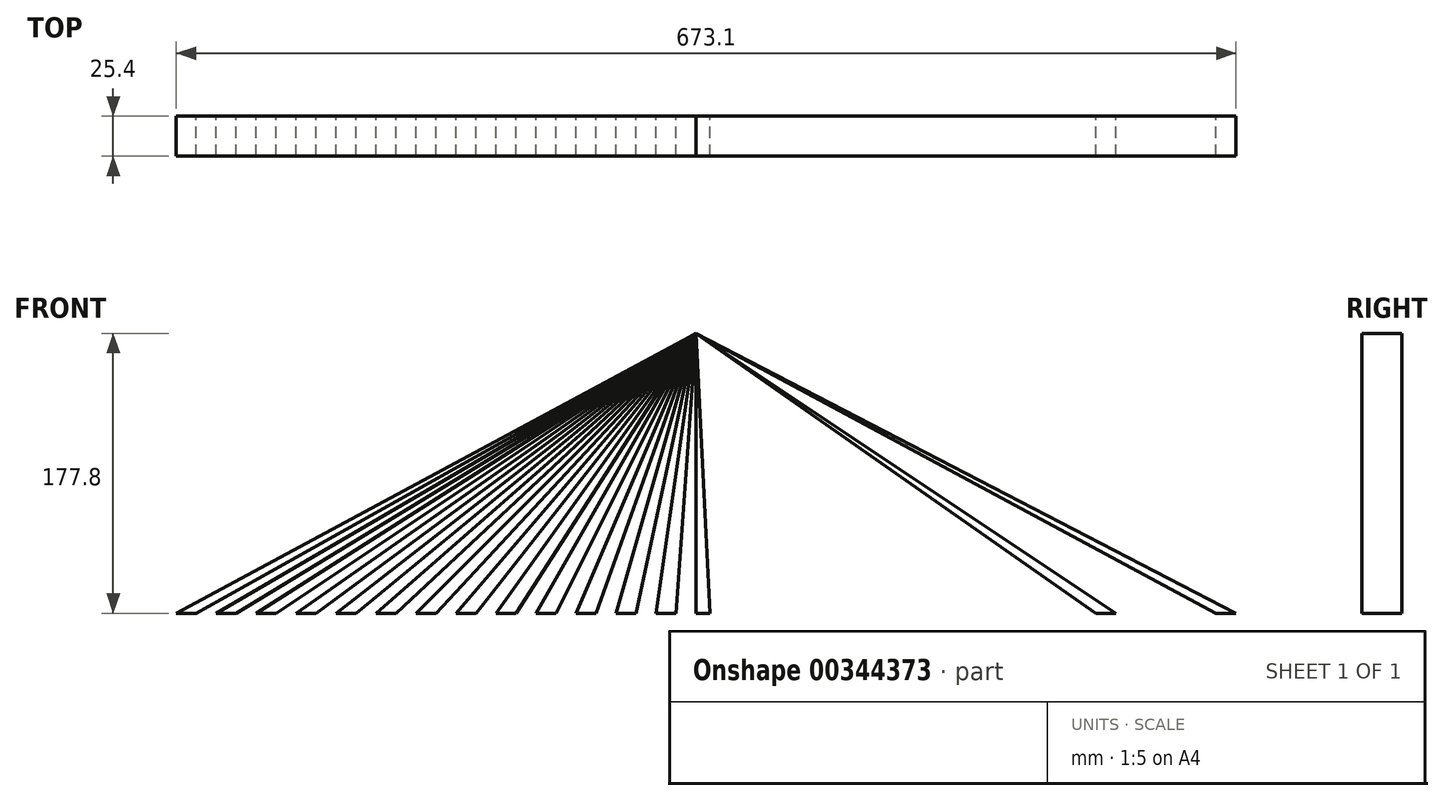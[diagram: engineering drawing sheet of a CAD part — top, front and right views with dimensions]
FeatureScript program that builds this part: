
annotation { "Feature Type Name" : "Feature", "Feature Type Description" : "" }
export const myFeature = defineFeature(function(context is Context, id is Id, definition is map)
    precondition{}
    {
        {
            var Q0;
            Q0=qCreatedBy(makeId("Front.planeOp"),FACE);
            var sketch = newSketch(context, id + "F0", { "sketchPlane" : qUnion([Q0])});
            skLineSegment(sketch, "E0", {"start": v(78.5, 0) * mm, "end": v(-175.5, 0) * mm});
            skLineSegment(sketch, "E1", {"start": v(-175.5, 0) * mm, "end": v(-175.5, 177.8) * mm});
            skLineSegment(sketch, "E2", {"start": v(-175.5, 177.8) * mm, "end": v(78.5, 0) * mm});
            skLineSegment(sketch, "E3", {"start": v(78.5, 0) * mm, "end": v(64.1, 0) * mm});
            skLineSegment(sketch, "E4", {"start": v(64.1, 0) * mm, "end": v(51.4, 0) * mm});
            skLineSegment(sketch, "E5", {"start": v(51.4, 0) * mm, "end": v(38.7, 0) * mm});
            skLineSegment(sketch, "E6", {"start": v(38.7, 0) * mm, "end": v(26, 0) * mm});
            skLineSegment(sketch, "E7", {"start": v(26, 0) * mm, "end": v(12.7, 0) * mm});
            skLineSegment(sketch, "E8", {"start": v(12.7, 0) * mm, "end": v(0, 0) * mm});
            skLineSegment(sketch, "E9", {"start": v(0, 0) * mm, "end": v(-12.7, 0) * mm});
            skLineSegment(sketch, "E10", {"start": v(-12.7, 0) * mm, "end": v(-25.4, 0) * mm});
            skLineSegment(sketch, "E11", {"start": v(-25.4, 0) * mm, "end": v(-38.1, 0) * mm});
            skLineSegment(sketch, "E12", {"start": v(-38.1, 0) * mm, "end": v(-48.5, 0) * mm});
            skLineSegment(sketch, "E13", {"start": v(-48.5, 0) * mm, "end": v(-64.04, 0) * mm});
            skLineSegment(sketch, "E14", {"start": v(-64.04, 0) * mm, "end": v(-77.66, 0) * mm});
            skLineSegment(sketch, "E15", {"start": v(-77.66, 0) * mm, "end": v(-89.19, 0) * mm});
            skLineSegment(sketch, "E16", {"start": v(-89.19, 0) * mm, "end": v(-102.8, 0) * mm});
            skLineSegment(sketch, "E17", {"start": v(-102.8, 0) * mm, "end": v(-118.17, 0) * mm});
            skLineSegment(sketch, "E18", {"start": v(-118.17, 0) * mm, "end": v(-131.45, 0) * mm});
            skLineSegment(sketch, "E19", {"start": v(-131.45, 0) * mm, "end": v(-144.02, 0) * mm});
            skLineSegment(sketch, "E20", {"start": v(-144.02, 0) * mm, "end": v(-155.55, 0) * mm});
            skLineSegment(sketch, "E21", {"start": v(-155.55, 0) * mm, "end": v(-166.72, 0) * mm});
            skLineSegment(sketch, "E22", {"start": v(-166.72, 0) * mm, "end": v(-175.5, 0) * mm});
            skLineSegment(sketch, "E23", {"start": v(-175.5, 177.8) * mm, "end": v(64.1, 0) * mm});
            skLineSegment(sketch, "E24", {"start": v(-175.5, 177.8) * mm, "end": v(51.4, 0) * mm});
            skLineSegment(sketch, "E25", {"start": v(-175.5, 177.8) * mm, "end": v(38.7, 0) * mm});
            skLineSegment(sketch, "E26", {"start": v(-175.5, 177.8) * mm, "end": v(26, 0) * mm});
            skLineSegment(sketch, "E27", {"start": v(-175.5, 177.8) * mm, "end": v(12.7, 0) * mm});
            skLineSegment(sketch, "E28", {"start": v(-175.5, 177.8) * mm, "end": v(0, 0) * mm});
            skLineSegment(sketch, "E29", {"start": v(-175.5, 177.8) * mm, "end": v(-12.7, 0) * mm});
            skLineSegment(sketch, "E30", {"start": v(-175.5, 177.8) * mm, "end": v(-25.4, 0) * mm});
            skLineSegment(sketch, "E31", {"start": v(-175.5, 177.8) * mm, "end": v(-38.1, 0) * mm});
            skLineSegment(sketch, "E32", {"start": v(-175.5, 177.8) * mm, "end": v(-48.5, 0) * mm});
            skLineSegment(sketch, "E33", {"start": v(-175.5, 177.8) * mm, "end": v(-64.04, 0) * mm});
            skLineSegment(sketch, "E34", {"start": v(-175.5, 177.8) * mm, "end": v(-77.66, 0) * mm});
            skLineSegment(sketch, "E35", {"start": v(-175.5, 177.8) * mm, "end": v(-89.19, 0) * mm});
            skLineSegment(sketch, "E36", {"start": v(-175.5, 177.8) * mm, "end": v(-102.8, 0) * mm});
            skLineSegment(sketch, "E37", {"start": v(-175.5, 177.8) * mm, "end": v(-118.17, 0) * mm});
            skLineSegment(sketch, "E38", {"start": v(-175.5, 177.8) * mm, "end": v(-131.45, 0) * mm});
            skLineSegment(sketch, "E39", {"start": v(-175.5, 177.8) * mm, "end": v(-144.02, 0) * mm});
            skLineSegment(sketch, "E40", {"start": v(-175.5, 177.8) * mm, "end": v(-155.55, 0) * mm});
            skLineSegment(sketch, "E41", {"start": v(-175.5, 177.8) * mm, "end": v(-166.72, 0) * mm});
            skLineSegment(sketch, "E42", {"start": v(78.5, 0) * mm, "end": v(154.7, 0) * mm});
            skLineSegment(sketch, "E43", {"start": v(78.5, 0) * mm, "end": v(91.2, 0) * mm});
            skLineSegment(sketch, "E44", {"start": v(91.2, 0) * mm, "end": v(103.9, 0) * mm});
            skLineSegment(sketch, "E45", {"start": v(103.9, 0) * mm, "end": v(116.6, 0) * mm});
            skLineSegment(sketch, "E46", {"start": v(116.6, 0) * mm, "end": v(129.3, 0) * mm});
            skLineSegment(sketch, "E47", {"start": v(129.3, 0) * mm, "end": v(142, 0) * mm});
            skLineSegment(sketch, "E48", {"start": v(-175.5, 177.8) * mm, "end": v(91.2, 0) * mm});
            skLineSegment(sketch, "E49", {"start": v(-175.5, 177.8) * mm, "end": v(103.9, 0) * mm});
            skLineSegment(sketch, "E50", {"start": v(-175.5, 177.8) * mm, "end": v(116.6, 0) * mm});
            skLineSegment(sketch, "E51", {"start": v(-175.5, 177.8) * mm, "end": v(129.3, 0) * mm});
            skLineSegment(sketch, "E52", {"start": v(-175.5, 177.8) * mm, "end": v(142, 0) * mm});
            skLineSegment(sketch, "E53", {"start": v(-175.5, 177.8) * mm, "end": v(154.7, 0) * mm});
            skLineSegment(sketch, "E54", {"start": v(154.7, 0) * mm, "end": v(167.4, 0) * mm});
            skLineSegment(sketch, "E55", {"start": v(-175.5, 177.8) * mm, "end": v(167.4, 0) * mm});
            skLineSegment(sketch, "E56", {"start": v(-175.5, 0) * mm, "end": v(-188.2, 0) * mm});
            skLineSegment(sketch, "E57", {"start": v(-188.2, 0) * mm, "end": v(-200.9, 0) * mm});
            skLineSegment(sketch, "E58", {"start": v(-200.9, 0) * mm, "end": v(-213.6, 0) * mm});
            skLineSegment(sketch, "E59", {"start": v(-213.6, 0) * mm, "end": v(-226.3, 0) * mm});
            skLineSegment(sketch, "E60", {"start": v(-226.3, 0) * mm, "end": v(-239, 0) * mm});
            skLineSegment(sketch, "E61", {"start": v(-239, 0) * mm, "end": v(-251.7, 0) * mm});
            skLineSegment(sketch, "E62", {"start": v(-251.7, 0) * mm, "end": v(-264.4, 0) * mm});
            skLineSegment(sketch, "E63", {"start": v(-264.4, 0) * mm, "end": v(-277.1, 0) * mm});
            skLineSegment(sketch, "E64", {"start": v(-277.1, 0) * mm, "end": v(-289.8, 0) * mm});
            skLineSegment(sketch, "E65", {"start": v(-289.8, 0) * mm, "end": v(-302.5, 0) * mm});
            skLineSegment(sketch, "E66", {"start": v(-175.5, 177.8) * mm, "end": v(-188.2, 0) * mm});
            skLineSegment(sketch, "E67", {"start": v(-175.5, 177.8) * mm, "end": v(-200.9, 0) * mm});
            skLineSegment(sketch, "E68", {"start": v(-175.5, 177.8) * mm, "end": v(-213.6, 0) * mm});
            skLineSegment(sketch, "E69", {"start": v(-175.5, 177.8) * mm, "end": v(-226.3, 0) * mm});
            skLineSegment(sketch, "E70", {"start": v(-175.5, 177.8) * mm, "end": v(-239, 0) * mm});
            skLineSegment(sketch, "E71", {"start": v(-175.5, 177.8) * mm, "end": v(-251.7, 0) * mm});
            skLineSegment(sketch, "E72", {"start": v(-175.5, 177.8) * mm, "end": v(-264.4, 0) * mm});
            skLineSegment(sketch, "E73", {"start": v(-175.5, 177.8) * mm, "end": v(-277.1, 0) * mm});
            skLineSegment(sketch, "E74", {"start": v(-175.5, 177.8) * mm, "end": v(-289.8, 0) * mm});
            skLineSegment(sketch, "E75", {"start": v(-175.5, 177.8) * mm, "end": v(-302.5, 0) * mm});
            skLineSegment(sketch, "E76", {"start": v(-302.5, 0) * mm, "end": v(-315.2, 0) * mm});
            skLineSegment(sketch, "E77", {"start": v(-315.2, 0) * mm, "end": v(-327.9, 0) * mm});
            skLineSegment(sketch, "E78", {"start": v(-327.9, 0) * mm, "end": v(-340.6, 0) * mm});
            skLineSegment(sketch, "E79", {"start": v(-340.6, 0) * mm, "end": v(-353.3, 0) * mm});
            skLineSegment(sketch, "E80", {"start": v(-353.3, 0) * mm, "end": v(-366, 0) * mm});
            skLineSegment(sketch, "E81", {"start": v(-366, 0) * mm, "end": v(-378.7, 0) * mm});
            skLineSegment(sketch, "E82", {"start": v(-378.7, 0) * mm, "end": v(-391.4, 0) * mm});
            skLineSegment(sketch, "E83", {"start": v(-175.5, 177.8) * mm, "end": v(-315.2, 0) * mm});
            skLineSegment(sketch, "E84", {"start": v(-175.5, 177.8) * mm, "end": v(-327.9, 0) * mm});
            skLineSegment(sketch, "E85", {"start": v(-175.5, 177.8) * mm, "end": v(-340.6, 0) * mm});
            skLineSegment(sketch, "E86", {"start": v(-175.5, 177.8) * mm, "end": v(-353.3, 0) * mm});
            skLineSegment(sketch, "E87", {"start": v(-175.5, 177.8) * mm, "end": v(-366, 0) * mm});
            skLineSegment(sketch, "E88", {"start": v(-175.5, 177.8) * mm, "end": v(-378.7, 0) * mm});
            skLineSegment(sketch, "E89", {"start": v(-175.5, 177.8) * mm, "end": v(-391.4, 0) * mm});
            skLineSegment(sketch, "E90", {"start": v(-391.4, 0) * mm, "end": v(-404.1, 0) * mm});
            skLineSegment(sketch, "E91", {"start": v(-404.1, 0) * mm, "end": v(-416.8, 0) * mm});
            skLineSegment(sketch, "E92", {"start": v(-416.8, 0) * mm, "end": v(-429.5, 0) * mm});
            skLineSegment(sketch, "E93", {"start": v(-429.5, 0) * mm, "end": v(-442.2, 0) * mm});
            skLineSegment(sketch, "E94", {"start": v(-442.2, 0) * mm, "end": v(-454.9, 0) * mm});
            skLineSegment(sketch, "E95", {"start": v(-454.9, 0) * mm, "end": v(-467.6, 0) * mm});
            skLineSegment(sketch, "E96", {"start": v(-467.6, 0) * mm, "end": v(-480.3, 0) * mm});
            skLineSegment(sketch, "E97", {"start": v(-175.5, 177.8) * mm, "end": v(-404.1, 0) * mm});
            skLineSegment(sketch, "E98", {"start": v(-175.5, 177.8) * mm, "end": v(-416.8, 0) * mm});
            skLineSegment(sketch, "E99", {"start": v(-175.5, 177.8) * mm, "end": v(-429.5, 0) * mm});
            skLineSegment(sketch, "E100", {"start": v(-175.5, 177.8) * mm, "end": v(-442.2, 0) * mm});
            skLineSegment(sketch, "E101", {"start": v(-175.5, 177.8) * mm, "end": v(-454.9, 0) * mm});
            skLineSegment(sketch, "E102", {"start": v(-175.5, 177.8) * mm, "end": v(-467.6, 0) * mm});
            skLineSegment(sketch, "E103", {"start": v(-175.5, 177.8) * mm, "end": v(-480.3, 0) * mm});
            skLineSegment(sketch, "E104", {"start": v(-480.3, 0) * mm, "end": v(-493, 0) * mm});
            skLineSegment(sketch, "E105", {"start": v(-493, 0) * mm, "end": v(-505.7, 0) * mm});
            skLineSegment(sketch, "E106", {"start": v(-175.5, 177.8) * mm, "end": v(-493, 0) * mm});
            skLineSegment(sketch, "E107", {"start": v(-505.7, 0) * mm, "end": v(-175.5, 177.8) * mm});
            skSolve(sketch);
        }
        {
            var Q0;
            Q0=makeQuery(id+"F0.imprint","IMPRINT",FACE,{"disambiguationData":[TD([[makeQuery(id+"F0.imprint","IMPRINT",EDGE,{"derivedFrom":sQuery(id+"F0.wireOp",EDGE,"E1")}),-1.0]])]});
            var Q1;
            Q1=makeQuery(id+"F0.imprint","IMPRINT",FACE,{"disambiguationData":[TD([[makeQuery(id+"F0.imprint","IMPRINT",EDGE,{"derivedFrom":sQuery(id+"F0.wireOp",EDGE,"E20")}),-1.0]])]});
            var Q2;
            Q2=makeQuery(id+"F0.imprint","IMPRINT",FACE,{"disambiguationData":[TD([[makeQuery(id+"F0.imprint","IMPRINT",EDGE,{"derivedFrom":sQuery(id+"F0.wireOp",EDGE,"E18")}),-1.0]])]});
            var Q3;
            Q3=makeQuery(id+"F0.imprint","IMPRINT",FACE,{"disambiguationData":[TD([[makeQuery(id+"F0.imprint","IMPRINT",EDGE,{"derivedFrom":sQuery(id+"F0.wireOp",EDGE,"E16")}),-1.0]])]});
            var Q4;
            Q4=makeQuery(id+"F0.imprint","IMPRINT",FACE,{"disambiguationData":[TD([[makeQuery(id+"F0.imprint","IMPRINT",EDGE,{"derivedFrom":sQuery(id+"F0.wireOp",EDGE,"E14")}),-1.0]])]});
            var Q5;
            Q5=makeQuery(id+"F0.imprint","IMPRINT",FACE,{"disambiguationData":[TD([[makeQuery(id+"F0.imprint","IMPRINT",EDGE,{"derivedFrom":sQuery(id+"F0.wireOp",EDGE,"E12")}),-1.0]])]});
            var Q6;
            Q6=makeQuery(id+"F0.imprint","IMPRINT",FACE,{"disambiguationData":[TD([[makeQuery(id+"F0.imprint","IMPRINT",EDGE,{"derivedFrom":sQuery(id+"F0.wireOp",EDGE,"E10")}),-1.0]])]});
            var Q7;
            Q7=makeQuery(id+"F0.imprint","IMPRINT",FACE,{"disambiguationData":[TD([[makeQuery(id+"F0.imprint","IMPRINT",EDGE,{"derivedFrom":sQuery(id+"F0.wireOp",EDGE,"E8")}),-1.0]])]});
            var Q8;
            Q8=makeQuery(id+"F0.imprint","IMPRINT",FACE,{"disambiguationData":[TD([[makeQuery(id+"F0.imprint","IMPRINT",EDGE,{"derivedFrom":sQuery(id+"F0.wireOp",EDGE,"E6")}),-1.0]])]});
            var Q9;
            Q9=makeQuery(id+"F0.imprint","IMPRINT",FACE,{"disambiguationData":[TD([[makeQuery(id+"F0.imprint","IMPRINT",EDGE,{"derivedFrom":sQuery(id+"F0.wireOp",EDGE,"E4")}),-1.0]])]});
            var Q10;
            Q10=makeQuery(id+"F0.imprint","IMPRINT",FACE,{"disambiguationData":[TD([[makeQuery(id+"F0.imprint","IMPRINT",EDGE,{"derivedFrom":sQuery(id+"F0.wireOp",EDGE,"E2")}),1.0]])]});
            var Q11;
            Q11=makeQuery(id+"F0.imprint","IMPRINT",FACE,{"disambiguationData":[TD([[makeQuery(id+"F0.imprint","IMPRINT",EDGE,{"derivedFrom":sQuery(id+"F0.wireOp",EDGE,"E45")}),1.0]])]});
            var Q12;
            Q12=makeQuery(id+"F0.imprint","IMPRINT",FACE,{"disambiguationData":[TD([[makeQuery(id+"F0.imprint","IMPRINT",EDGE,{"derivedFrom":sQuery(id+"F0.wireOp",EDGE,"E47")}),1.0]])]});
            var Q13;
            Q13=makeQuery(id+"F0.imprint","IMPRINT",FACE,{"disambiguationData":[TD([[makeQuery(id+"F0.imprint","IMPRINT",EDGE,{"derivedFrom":sQuery(id+"F0.wireOp",EDGE,"E53")}),1.0]])]});
            var Q14;
            Q14=makeQuery(id+"F0.imprint","IMPRINT",FACE,{"disambiguationData":[TD([[makeQuery(id+"F0.imprint","IMPRINT",EDGE,{"derivedFrom":sQuery(id+"F0.wireOp",EDGE,"E57")}),-1.0]])]});
            var Q15;
            Q15=makeQuery(id+"F0.imprint","IMPRINT",FACE,{"disambiguationData":[TD([[makeQuery(id+"F0.imprint","IMPRINT",EDGE,{"derivedFrom":sQuery(id+"F0.wireOp",EDGE,"E59")}),-1.0]])]});
            var Q16;
            Q16=makeQuery(id+"F0.imprint","IMPRINT",FACE,{"disambiguationData":[TD([[makeQuery(id+"F0.imprint","IMPRINT",EDGE,{"derivedFrom":sQuery(id+"F0.wireOp",EDGE,"E61")}),-1.0]])]});
            var Q17;
            Q17=makeQuery(id+"F0.imprint","IMPRINT",FACE,{"disambiguationData":[TD([[makeQuery(id+"F0.imprint","IMPRINT",EDGE,{"derivedFrom":sQuery(id+"F0.wireOp",EDGE,"E63")}),-1.0]])]});
            var Q18;
            Q18=makeQuery(id+"F0.imprint","IMPRINT",FACE,{"disambiguationData":[TD([[makeQuery(id+"F0.imprint","IMPRINT",EDGE,{"derivedFrom":sQuery(id+"F0.wireOp",EDGE,"E65")}),-1.0]])]});
            var Q19;
            Q19=makeQuery(id+"F0.imprint","IMPRINT",FACE,{"disambiguationData":[TD([[makeQuery(id+"F0.imprint","IMPRINT",EDGE,{"derivedFrom":sQuery(id+"F0.wireOp",EDGE,"E77")}),-1.0]])]});
            var Q20;
            Q20=makeQuery(id+"F0.imprint","IMPRINT",FACE,{"disambiguationData":[TD([[makeQuery(id+"F0.imprint","IMPRINT",EDGE,{"derivedFrom":sQuery(id+"F0.wireOp",EDGE,"E79")}),-1.0]])]});
            var Q21;
            Q21=makeQuery(id+"F0.imprint","IMPRINT",FACE,{"disambiguationData":[TD([[makeQuery(id+"F0.imprint","IMPRINT",EDGE,{"derivedFrom":sQuery(id+"F0.wireOp",EDGE,"E81")}),-1.0]])]});
            var Q22;
            Q22=makeQuery(id+"F0.imprint","IMPRINT",FACE,{"disambiguationData":[TD([[makeQuery(id+"F0.imprint","IMPRINT",EDGE,{"derivedFrom":sQuery(id+"F0.wireOp",EDGE,"E89")}),-1.0]])]});
            var Q23;
            Q23=makeQuery(id+"F0.imprint","IMPRINT",FACE,{"disambiguationData":[TD([[makeQuery(id+"F0.imprint","IMPRINT",EDGE,{"derivedFrom":sQuery(id+"F0.wireOp",EDGE,"E92")}),-1.0]])]});
            var Q24;
            Q24=makeQuery(id+"F0.imprint","IMPRINT",FACE,{"disambiguationData":[TD([[makeQuery(id+"F0.imprint","IMPRINT",EDGE,{"derivedFrom":sQuery(id+"F0.wireOp",EDGE,"E94")}),-1.0]])]});
            var Q25;
            Q25=makeQuery(id+"F0.imprint","IMPRINT",FACE,{"disambiguationData":[TD([[makeQuery(id+"F0.imprint","IMPRINT",EDGE,{"derivedFrom":sQuery(id+"F0.wireOp",EDGE,"E96")}),-1.0]])]});
            var Q26;
            Q26=makeQuery(id+"F0.imprint","IMPRINT",FACE,{"disambiguationData":[TD([[makeQuery(id+"F0.imprint","IMPRINT",EDGE,{"derivedFrom":sQuery(id+"F0.wireOp",EDGE,"E105")}),-1.0]])]});
            extrude(context, id + "F1", {"entities" : qUnion([Q0, Q1, Q2, Q3, Q4, Q5, Q6, Q7, Q8, Q9, Q10, Q11, Q12, Q13, Q14, Q15, Q16, Q17, Q18, Q19, Q20, Q21, Q22, Q23, Q24, Q25, Q26]), "depth" : 25.4 * mm});
        }
    });
